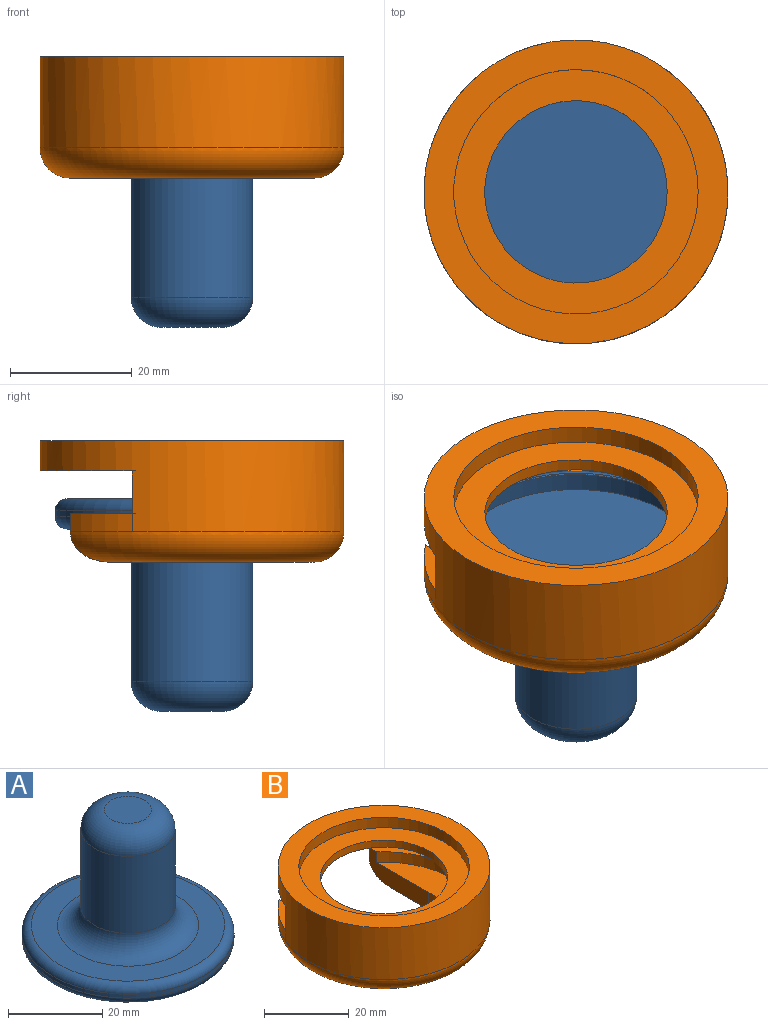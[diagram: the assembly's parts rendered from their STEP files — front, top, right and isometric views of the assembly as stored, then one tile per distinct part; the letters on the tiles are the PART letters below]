
ASSEMBLY  parts=2 mates=1
PART A: 11 faces, bbox 48.7x48.7x35 mm
  f0: plane 41x41mm, normal (0,0,1), area 613.4mm2, adj f7,f10
  f1: cylinder r=10mm len=20mm, axis (0,0,-1), area 1256.6mm2, adj f7,f8
  f2: plane 10x10mm, normal (0,0,1), area 78.5mm2, adj f8
  f3: plane 40.2x40.2mm, normal (0,0,-1), area 1269.2mm2, adj f4
  f4: cylinder r=20.1mm len=40.2mm, axis (0,0,-1), area 378.9mm2, adj f3,f5
  f5: plane 41x41mm, normal (0,0,-1), area 51mm2, adj f4,f9
  f6: cylinder r=22.5mm len=45mm, axis (0,0,-1), area 141.4mm2, adj f9,f10
  f7: torus R=15mm, axis (0,0,-1), area 583.1mm2, adj f0,f1
  f8: torus R=5mm, axis (0,0,-1), area 403.8mm2, adj f1,f2
  f9: torus R=20.5mm, axis (0,0,-1), area 429.8mm2, adj f5,f6
  f10: torus R=20.5mm, axis (0,0,-1), area 429.8mm2, adj f0,f6
PART B: 18 faces, bbox 54.1x52.1x20 mm
  f0: cylinder r=15mm len=30mm, axis (0,0,-1), area 235.6mm2, adj f4,f11,f12,f16
  f1: cylinder r=25mm len=50mm, axis (0,0,-1), area 1811.5mm2, adj f2,f3,f8,f9,f12,f13,f14,f17
  f2: cylinder r=25mm len=10.2mm, axis (0,0,-1), area 39.3mm2, adj f1,f10,f11,f17
  f3: plane 50x50mm, normal (0,0,1), area 694.3mm2, adj f1,f5
  f4: plane 40x33.23mm, normal (0,0,-1), area 365.6mm2, adj f0,f11,f12,f17
  f5: cylinder r=20.1mm len=40.2mm, axis (0,0,1), area 378.9mm2, adj f3,f6
  f6: plane 40.2x40.2mm, normal (0,0,1), area 562.4mm2, adj f5,f7
  f7: cylinder r=15mm len=30mm, axis (0,0,-1), area 188.5mm2, adj f6,f14
  f8: plane 9.8x7mm, normal (-1,0,0), area 68.6mm2, adj f1,f13,f14,f15
  f9: plane 9.8x7mm, normal (1,0,0), area 68.6mm2, adj f1,f10,f14,f15
  f10: plane 20x8mm, normal (0,0,1), area 29.8mm2, adj f2,f9,f11,f15
  f11: plane 20x8mm, normal (1,0,0), area 100.8mm2, adj f0,f2,f4,f10,f15,f16,f17
  f12: plane 20x8mm, normal (-1,0,0), area 100.8mm2, adj f0,f1,f4,f13,f15,f16,f17
  f13: plane 20x8mm, normal (0,0,1), area 29.8mm2, adj f1,f8,f12,f15
  f14: plane 48x46mm, normal (0,0,-1), area 1079.5mm2, adj f1,f7,f8,f9,f15
  f15: cylinder r=23mm len=46mm, axis (0,0,1), area 841.3mm2, adj f8,f9,f10,f11,f12,f13,f14,f16
  f16: plane 46x40.44mm, normal (0,0,1), area 671.1mm2, adj f0,f11,f12,f15
  f17: torus R=20mm, axis (0,0,1), area 887.2mm2, adj f1,f2,f4,f11,f12
PLACE A rot(axis=(0,1,0),180deg) t=(0.31,1.72,10.44)mm
PLACE B t=(0.31,1.72,0)mm
MATE slider A.f1 <-> B.f1  axis (0,0,1) through (0.31,1.72,7.44)mm
